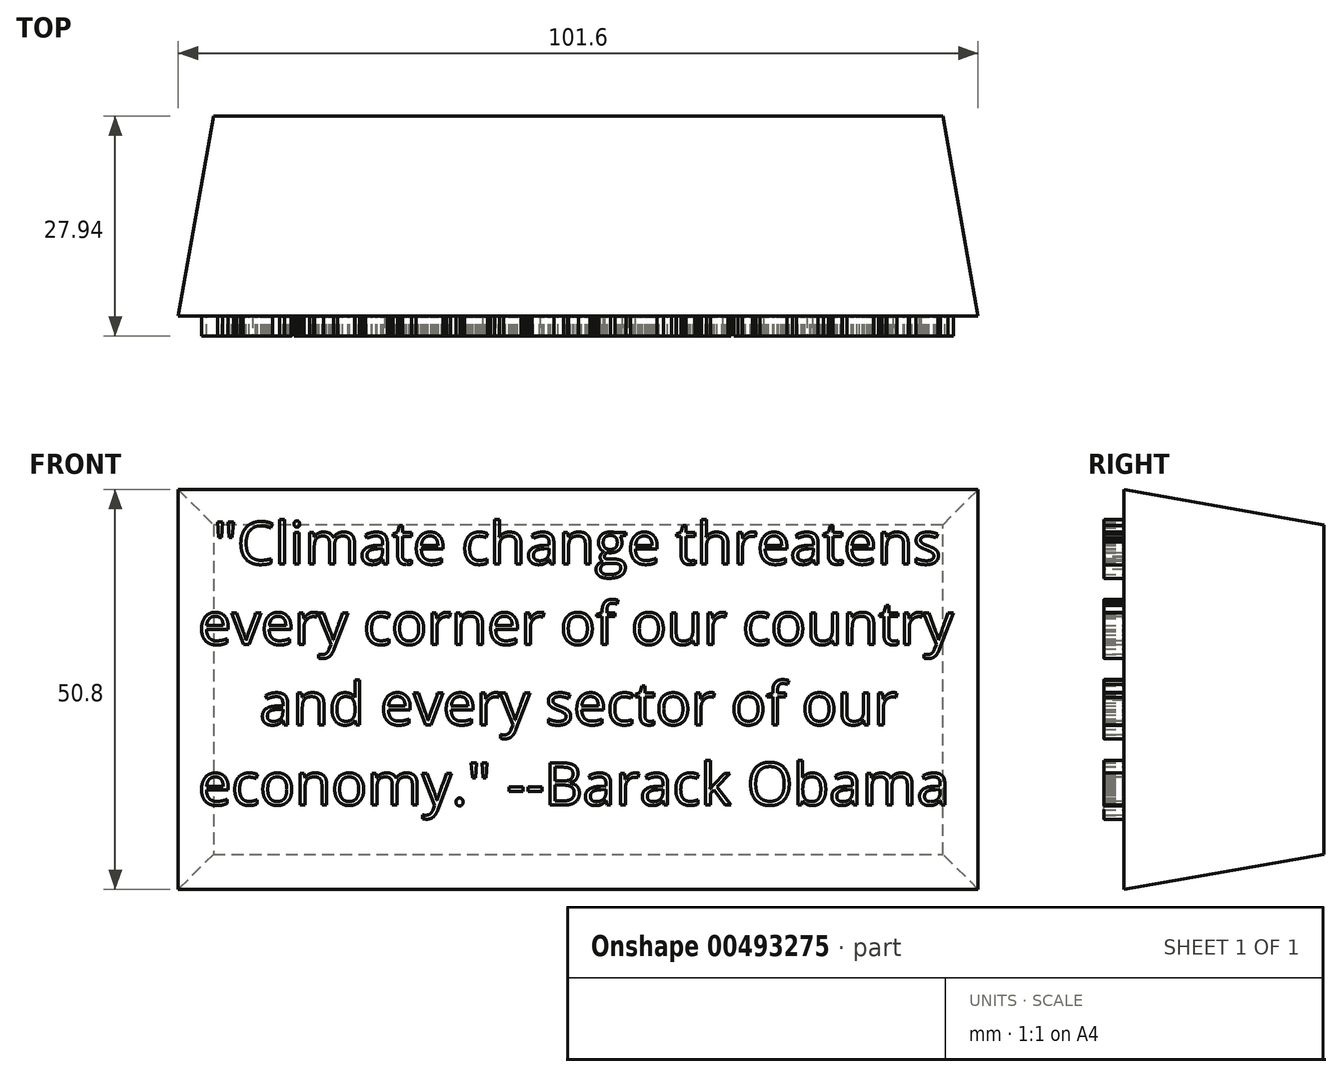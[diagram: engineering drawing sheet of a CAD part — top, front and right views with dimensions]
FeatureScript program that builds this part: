
annotation { "Feature Type Name" : "Feature", "Feature Type Description" : "" }
export const myFeature = defineFeature(function(context is Context, id is Id, definition is map)
    precondition{}
    {
        {
            var Q0;
            Q0=qCreatedBy(makeId("Front.planeOp"),FACE);
            var sketch = newSketch(context, id + "F0", { "sketchPlane" : qUnion([Q0])});
            skLineSegment(sketch, "E0.bottom", {"start": v(-101.6, 50.8) * mm, "end": v(0, 50.8) * mm});
            skLineSegment(sketch, "E0.top", {"start": v(-101.6, 0) * mm, "end": v(0, 0) * mm});
            skLineSegment(sketch, "E0.left", {"start": v(-101.6, 50.8) * mm, "end": v(-101.6, 0) * mm});
            skLineSegment(sketch, "E0.right", {"start": v(0, 50.8) * mm, "end": v(0, 0) * mm});
            skSolve(sketch);
        }
        {
            var Q0;
            Q0=qSketchRegion(id+"F0",true);
            extrude(context, id + "F1", {"entities" : qUnion([Q0]), "oppositeDirection" : true, "depth" : 25.4 * mm, "hasDraft" : true, "draftAngle" : 10 * degree, "draftPullDirection" : true});
        }
        {
            var Q0;
            Q0=makeQuery(id+"F1.opExtrude","CAP_FACE",FACE,{"disambiguationData":[OSD([sQuery(id+"F0.wireOp",EDGE,"E0.bottom"),sQuery(id+"F0.wireOp",EDGE,"E0.top"),sQuery(id+"F0.wireOp",EDGE,"E0.left"),sQuery(id+"F0.wireOp",EDGE,"E0.right")])],"isStart":true});
            var sketch = newSketch(context, id + "F2", { "sketchPlane" : qUnion([Q0])});
            skText(sketch, "E1", { "text": " \"Climate change threatens\nevery corner of our country\n    and every sector of our\neconomy.\" --Barack Obama", "fontName": "OpenSans-Regular.ttf"});
            const initialGuessF2  = {"E1": [-0.09906, 0.04132, 1, 0, 0.0054]};
            skSetInitialGuess(sketch, initialGuessF2);
            skSolve(sketch);
        }
        {
            var Q0;
            Q0=qSketchRegion(id+"F2",true);
            extrude(context, id + "F3", {"entities" : qUnion([Q0]), "operationType" : NewBodyOperationType.ADD, "depth" : 2.54 * mm});
        }
    });
